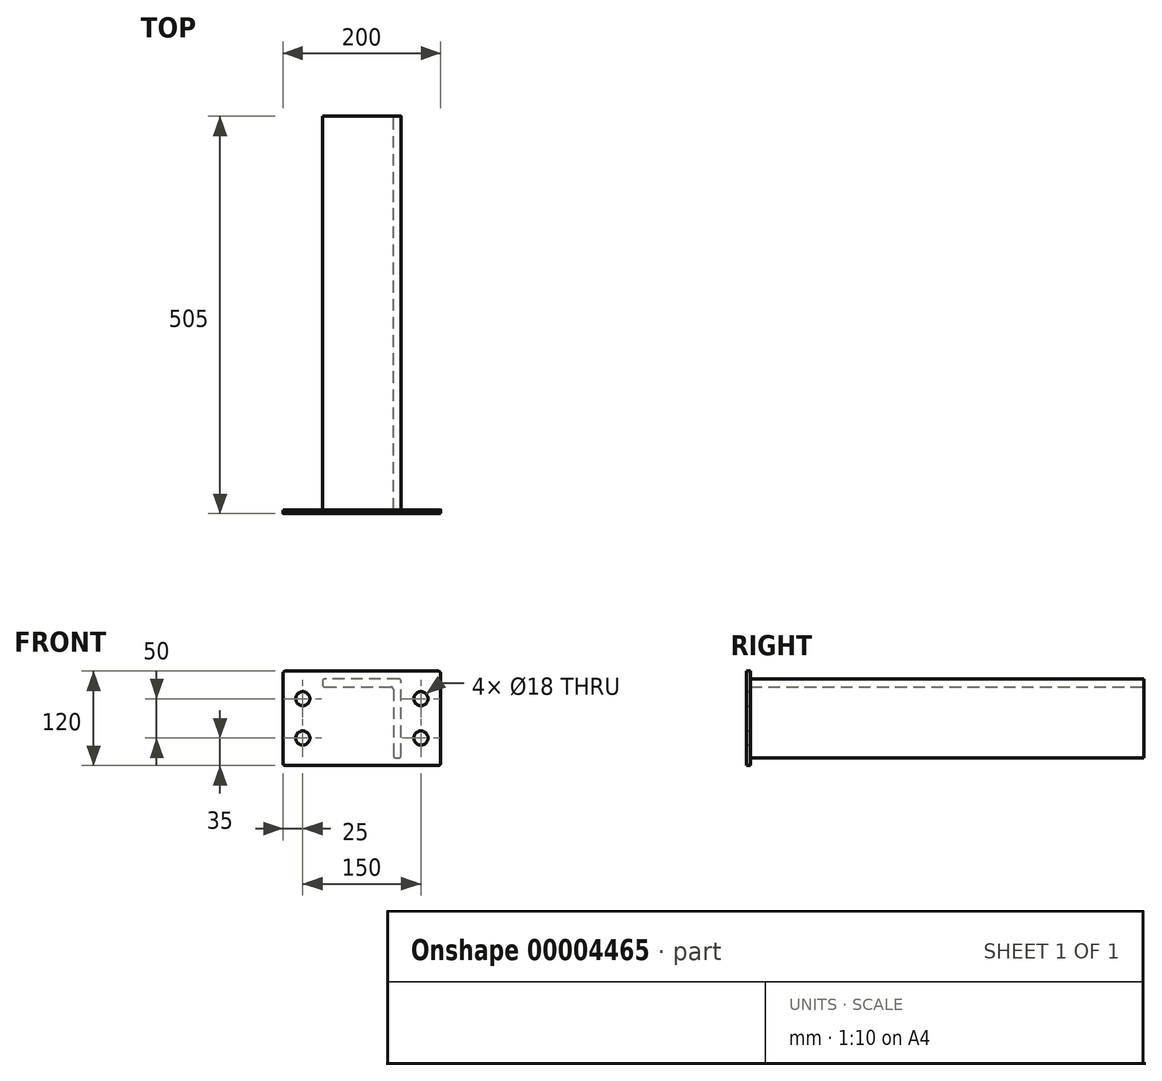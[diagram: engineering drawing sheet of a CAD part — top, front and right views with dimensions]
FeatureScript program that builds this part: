
annotation { "Feature Type Name" : "Feature", "Feature Type Description" : "" }
export const myFeature = defineFeature(function(context is Context, id is Id, definition is map)
    precondition{}
    {
        {
            var Q0;
            Q0=qCreatedBy(makeId("Front.planeOp"),FACE);
            var sketch = newSketch(context, id + "F0", { "sketchPlane" : qUnion([Q0])});
            skLineSegment(sketch, "E0", {"start": v(0, 3) * mm, "end": v(0, 97) * mm});
            skLineSegment(sketch, "E1", {"start": v(-3, 100) * mm, "end": v(-97, 100) * mm});
            skLineSegment(sketch, "E2", {"start": v(-100, 97) * mm, "end": v(-100, 93) * mm});
            skLineSegment(sketch, "E3", {"start": v(-97, 90) * mm, "end": v(-13, 90) * mm});
            skLineSegment(sketch, "E4", {"start": v(-10, 87) * mm, "end": v(-10, 3) * mm});
            skLineSegment(sketch, "E5", {"start": v(-7, 0) * mm, "end": v(-3, 0) * mm});
            skPoint(sketch, "E6.visualSharp", {"position": v(0, 100) * mm});
            skArc(sketch, "E6.filletArc", {"start": v(0, 97) * mm, "mid": v(-0.88, 99.12) * mm, "end": v(-3, 100) * mm});
            skPoint(sketch, "E7.visualSharp", {"position": v(-10, 90) * mm});
            skArc(sketch, "E7.filletArc", {"start": v(-10, 87) * mm, "mid": v(-10.88, 89.12) * mm, "end": v(-13, 90) * mm});
            skPoint(sketch, "E8.visualSharp", {"position": v(0, 0) * mm});
            skArc(sketch, "E8.filletArc", {"start": v(-3, 0) * mm, "mid": v(-0.88, 0.88) * mm, "end": v(0, 3) * mm});
            skPoint(sketch, "E9.visualSharp", {"position": v(-10, 0) * mm});
            skArc(sketch, "E9.filletArc", {"start": v(-10, 3) * mm, "mid": v(-9.12, 0.88) * mm, "end": v(-7, 0) * mm});
            skPoint(sketch, "E10.visualSharp", {"position": v(-100, 90) * mm});
            skArc(sketch, "E10.filletArc", {"start": v(-100, 93) * mm, "mid": v(-99.12, 90.88) * mm, "end": v(-97, 90) * mm});
            skPoint(sketch, "E11.visualSharp", {"position": v(-100, 100) * mm});
            skArc(sketch, "E11.filletArc", {"start": v(-97, 100) * mm, "mid": v(-99.12, 99.12) * mm, "end": v(-100, 97) * mm});
            skSolve(sketch);
        }
        {
            var Q0;
            Q0=makeQuery(id+"F0.imprint","IMPRINT",FACE,{"disambiguationData":[TD([[makeQuery(id+"F0.imprint","IMPRINT",EDGE,{"derivedFrom":sQuery(id+"F0.wireOp",EDGE,"E0")}),1.0]])]});
            extrude(context, id + "F1", {"entities" : qUnion([Q0]), "depth" : 500 * mm});
        }
        {
            var Q0;
            Q0=makeQuery(id+"F1.opExtrude","CAP_FACE",FACE,{"disambiguationData":[OSD([sQuery(id+"F0.wireOp",EDGE,"E0"),sQuery(id+"F0.wireOp",EDGE,"E1"),sQuery(id+"F0.wireOp",EDGE,"E2"),sQuery(id+"F0.wireOp",EDGE,"E3"),sQuery(id+"F0.wireOp",EDGE,"E4"),sQuery(id+"F0.wireOp",EDGE,"E5"),sQuery(id+"F0.wireOp",EDGE,"E6.filletArc"),sQuery(id+"F0.wireOp",EDGE,"E7.filletArc"),sQuery(id+"F0.wireOp",EDGE,"E8.filletArc"),sQuery(id+"F0.wireOp",EDGE,"E9.filletArc"),sQuery(id+"F0.wireOp",EDGE,"E10.filletArc"),sQuery(id+"F0.wireOp",EDGE,"E11.filletArc")])],"isStart":false});
            var sketch = newSketch(context, id + "F2", { "sketchPlane" : qUnion([Q0])});
            skLineSegment(sketch, "E12.bottom", {"start": v(47, -10) * mm, "end": v(-147, -10) * mm});
            skLineSegment(sketch, "E12.top", {"start": v(47, 110) * mm, "end": v(-147, 110) * mm});
            skLineSegment(sketch, "E12.left", {"start": v(50, -7) * mm, "end": v(50, 107) * mm});
            skLineSegment(sketch, "E12.right", {"start": v(-150, -7) * mm, "end": v(-150, 107) * mm});
            skLineSegment(sketch, "E13", {"start": v(-50, 110) * mm, "end": v(-50, -10) * mm, "construction": true});
            skPoint(sketch, "E14", {"position": v(-50, 100) * mm});
            skPoint(sketch, "E15", {"position": v(0, 50) * mm});
            skLineSegment(sketch, "E16", {"start": v(-150, 50) * mm, "end": v(50, 50) * mm, "construction": true});
            skCircle(sketch, "E17", {"center": v(-125, 75) * mm, "radius": 9 * mm});
            skLineSegment(sketch, "E18.bottom", {"start": v(-125, 75) * mm, "end": v(25, 75) * mm, "construction": true});
            skLineSegment(sketch, "E18.top", {"start": v(-125, 25) * mm, "end": v(25, 25) * mm, "construction": true});
            skLineSegment(sketch, "E18.left", {"start": v(-125, 75) * mm, "end": v(-125, 25) * mm, "construction": true});
            skLineSegment(sketch, "E18.right", {"start": v(25, 75) * mm, "end": v(25, 25) * mm, "construction": true});
            skPoint(sketch, "E19", {"position": v(25, 50) * mm});
            skPoint(sketch, "E20", {"position": v(-50, 25) * mm});
            skCircle(sketch, "E21", {"center": v(25, 75) * mm, "radius": 9 * mm});
            skCircle(sketch, "E22", {"center": v(-125, 25) * mm, "radius": 9 * mm});
            skCircle(sketch, "E23", {"center": v(25, 25) * mm, "radius": 9 * mm});
            skPoint(sketch, "E24.visualSharp", {"position": v(-150, 110) * mm});
            skArc(sketch, "E24.filletArc", {"start": v(-147, 110) * mm, "mid": v(-149.12, 109.12) * mm, "end": v(-150, 107) * mm});
            skPoint(sketch, "E25.visualSharp", {"position": v(50, 110) * mm});
            skArc(sketch, "E25.filletArc", {"start": v(50, 107) * mm, "mid": v(49.12, 109.12) * mm, "end": v(47, 110) * mm});
            skPoint(sketch, "E26.visualSharp", {"position": v(50, -10) * mm});
            skArc(sketch, "E26.filletArc", {"start": v(47, -10) * mm, "mid": v(49.12, -9.12) * mm, "end": v(50, -7) * mm});
            skPoint(sketch, "E27.visualSharp", {"position": v(-150, -10) * mm});
            skArc(sketch, "E27.filletArc", {"start": v(-150, -7) * mm, "mid": v(-149.12, -9.12) * mm, "end": v(-147, -10) * mm});
            skSolve(sketch);
        }
        {
            var Q0;
            {var subQ11=makeQuery(id+"F2.imprint","IMPRINT",EDGE,{"derivedFrom":makeQuery(id+"F1.opExtrude","CAP_EDGE",EDGE,{"disambiguationData":[OSD([sQuery(id+"F0.wireOp",EDGE,"E0")])],"isStart":false})});Q0=qUnion([makeQuery(id+"F2.imprint","IMPRINT",FACE,{"disambiguationData":[TD([[subQ11,1.0]])]}),makeQuery(id+"F2.imprint","IMPRINT",FACE,{"disambiguationData":[TD([[makeQuery(id+"F2.imprint","IMPRINT",EDGE,{"derivedFrom":sQuery(id+"F2.wireOp",EDGE,"E12.bottom")}),-1.0]])]})]);}
            extrude(context, id + "F3", {"entities" : qUnion([Q0]), "depth" : 5 * mm});
        }
    });
